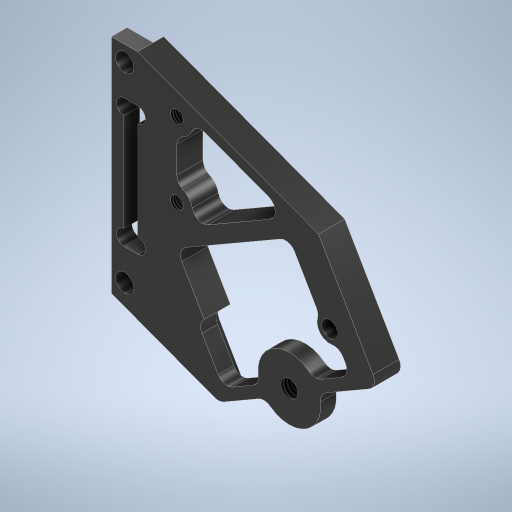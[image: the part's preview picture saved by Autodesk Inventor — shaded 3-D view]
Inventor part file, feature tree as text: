
AUTODESK INVENTOR PART (.ipt)
format: ipt  version: 2024.2 (Build 282272000, 272)  size: 419,328 bytes
history: native  units: mm
features: extrude x2, fillet x2, hole x2, other x1, sketch x1
ambient origin geometry x8: Origin, YZ Plane, XZ Plane, XY Plane, X Axis, Y Axis, Z Axis, Center Point
bodies: Solid1 (feature_tree)
feature tree (8):
  other  "ShoulderSideFrameBasis.ipt"
  extrude  "Extrusion1"  Depth=5.0mm TaperAngle=0.0deg
  extrude  "Extrusion2"  Depth=2.0mm TaperAngle=0.0deg
  fillet  "Inner-R2"  Radius=2.0mm
  fillet  "Outer-R2"  Radius=2.0mm
  hole  "Phi3.1"  [1 undecoded]
  hole  "Phi3.5"  [1 undecoded]
  sketch  "Sketch1"  dims[d0=10.0mm d1=5.0mm d2=0.0mm d3=2.0mm d4=0.0mm d5=2.0mm d8=3.242mm d9=8.0mm d10=4.0mm d11=2.0mm d12=90.0deg d13=8.0mm d14=20.594885mm d15=3.1mm d16=8.0mm d17=4.0mm d18=2.0mm d19=90.0deg d20=11.8mm d21=20.594885mm d22=2.0mm d23=3.5mm d24=6.0mm d25=4.0mm d26=2.0mm d27=90.0deg d28=8.0mm d29=20.594885mm d30=2.459mm d31=6.0mm d32=4.0mm d33=2.0mm d34=90.0deg d35=8.0mm d36=20.594885mm d37=0.0mm d38=0.0mm d39=0.0mm d40=0.0mm]
note: 2 required parameter values undecoded (feature->parameter linkage not recoverable at this tier; creation-order binding heuristic only, values carry confidence <= 0.55)
